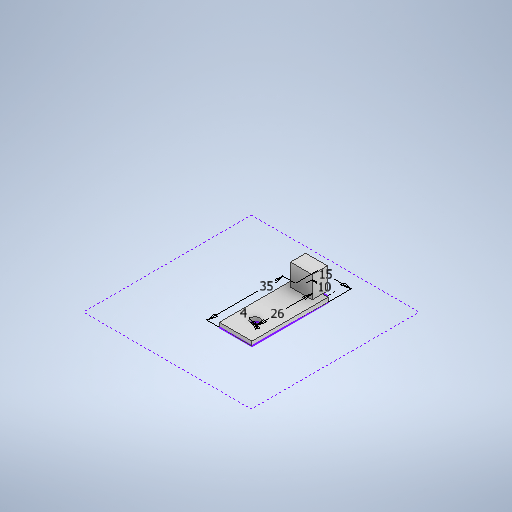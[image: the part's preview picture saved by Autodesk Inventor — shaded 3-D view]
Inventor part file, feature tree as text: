
AUTODESK INVENTOR PART (.ipt)
format: ipt  version: 2025.1 (Build 291241000, 241)  size: 273,408 bytes
history: native  units: mm
features: extrude x2, sketch x1, other x1
ambient origin geometry x8: Origin, YZ Plane, XZ Plane, XY Plane, X Axis, Y Axis, Z Axis, Center Point
bodies: Solid1 (feature_tree)
feature tree (4):
  sketch  "Sketch1"  dims[d6=35.0mm d9=15.0mm d11=4.0mm d21=26.0mm d26=10.0mm d28=2.0mm d29=0.0mm d30=10.0mm d31=0.0mm]
  extrude  "Extrusion1"  Depth=15.0mm
  extrude  "Extrusion2"  Depth=10.0mm
  other  "Image1"
